# Revit family: Indoor_Pendant Lamp_Santa&Cole_Moaré Liviana
name_source: partatom
category: Luminarias
revit_build: Autodesk Revit 2018 (Build: 20190510_1515(x64)
units: mm (PartAtom-declared; Revit-internal decimal feet)

## family parameters
Anfitrión = Cara
Compartido = No
Corte con vacíos al cargar = No
Cota de conector redondo = Diámetro de uso
Origen de luz = Sí
Punto de cálculo de habitación = No
Tipo de pieza = Normal

## types (2) — shared parameters
Assembly Instructions - CE = https://www.santacole.com
Assembly Instructions - UL = https://www.santacole.com
Cambio de temperatura de color de luz atenuada = <Ninguno>
Carga aparente = 12 W
Elevación por defecto = 1219 mm
Fabricante = Santa & Cole
Filtro de color = 16777215
Lampshade Material = <Por categoría>
Load = 12 W
Manufacturer website = http://www.santacole.com
Modelo = Moaré Liviana
Technical Information = https://www.santacole.com
URL = https://www.santacole.com
Voltaje (90-305 V) = 220 V
Ángulo de inclinación = -90.00°

## per-type parameters (varying)
| type | Archivo de red fotométrica | Code | Visibility_Moaré Liviana M | Visibility_Moaré Liviana S |
| Moaré Liviana M | MREML3.IES | SISxx+MREML3 | Sí | No |
| Moaré Liviana S | MRESL3.IES | SISxx+MRESL3 | No | Sí |

## geometry (parser evidence)
native form markers: Sweep x2
no freeform markers — native parametric forms only
